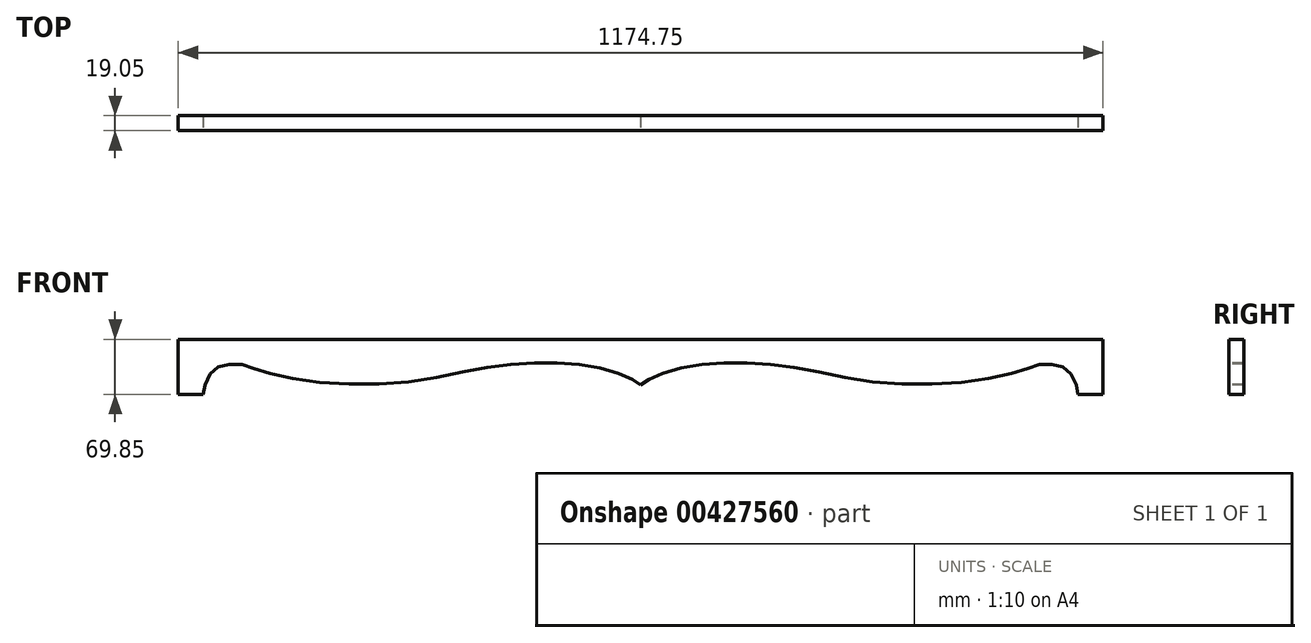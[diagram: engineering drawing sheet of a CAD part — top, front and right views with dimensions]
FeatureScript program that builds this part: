
annotation { "Feature Type Name" : "Feature", "Feature Type Description" : "" }
export const myFeature = defineFeature(function(context is Context, id is Id, definition is map)
    precondition{}
    {
        {
            var Q0;
            Q0=qCreatedBy(makeId("Front.planeOp"),FACE);
            var sketch = newSketch(context, id + "F0", { "sketchPlane" : qUnion([Q0])});
            skLineSegment(sketch, "E0.bottom", {"start": v(0, 0) * mm, "end": v(1174.75, 0) * mm});
            skLineSegment(sketch, "E0.top", {"start": v(0, 69.85) * mm, "end": v(1174.75, 69.85) * mm});
            skLineSegment(sketch, "E0.left", {"start": v(0, 0) * mm, "end": v(0, 69.85) * mm});
            skLineSegment(sketch, "E0.right", {"start": v(1174.75, 0) * mm, "end": v(1174.75, 69.85) * mm});
            skSolve(sketch);
        }
        {
            var Q0;
            Q0 = qSketchRegion(id + "F0", true);
            extrude(context, id + "F1", {"entities" : qUnion([Q0]), "depth" : 19.05 * mm});
        }
        {
            var Q0;
            Q0=makeQuery(id+"F1.opExtrude","CAP_FACE",FACE,{"disambiguationData":[OSD([sQuery(id+"F0.wireOp",EDGE,"E0.bottom"),sQuery(id+"F0.wireOp",EDGE,"E0.top"),sQuery(id+"F0.wireOp",EDGE,"E0.left"),sQuery(id+"F0.wireOp",EDGE,"E0.right")])],"isStart":false});
            var sketch = newSketch(context, id + "F2", { "sketchPlane" : qUnion([Q0])});
            skLineSegment(sketch, "E1", {"start": v(587.38, 69.85) * mm, "end": v(587.38, 0) * mm});
            skFitSpline(sketch, "E2", {"points": [v(31.64, 0) * mm, v(34.2, 12.66) * mm, v(44.37, 30.48) * mm, v(57.1, 36.42) * mm, v(79.16, 38.11) * mm, v(100.37, 31.32) * mm, v(172.5, 16.05) * mm, v(294.69, 16.05) * mm, v(391.42, 33.87) * mm, v(468.63, 39.8) * mm, v(534.82, 33.87) * mm, v(575.55, 19.44) * mm, v(587.38, 11.8) * mm], "startDerivative": vector(30.7, 255.74) * mm, "endDerivative": vector(206.13, -152.13) * mm});
            skFitSpline(sketch, "E3.MirrorCS", {"points": [v(1143.1, 0) * mm, v(1140.56, 12.66) * mm, v(1130.38, 30.48) * mm, v(1117.65, 36.42) * mm, v(1095.59, 38.11) * mm, v(1074.38, 31.32) * mm, v(1002.25, 16.05) * mm, v(880.06, 16.05) * mm, v(783.33, 33.87) * mm, v(706.12, 39.8) * mm, v(639.93, 33.87) * mm, v(599.2, 19.44) * mm, v(587.38, 11.8) * mm], "startDerivative": vector(-30.7, 255.74) * mm, "endDerivative": vector(-206.13, -152.13) * mm});
            skLineSegment(sketch, "E4", {"start": v(31.64, 0) * mm, "end": v(1143.1, 0) * mm});
            skSolve(sketch);
        }
        {
            var Q0;
            Q0 = qSketchRegion(id + "F2", true);
            extrude(context, id + "F3", {"entities" : qUnion([Q0]), "operationType" : NewBodyOperationType.REMOVE, "oppositeDirection" : true, "depth" : 25.4 * mm});
        }
    });
